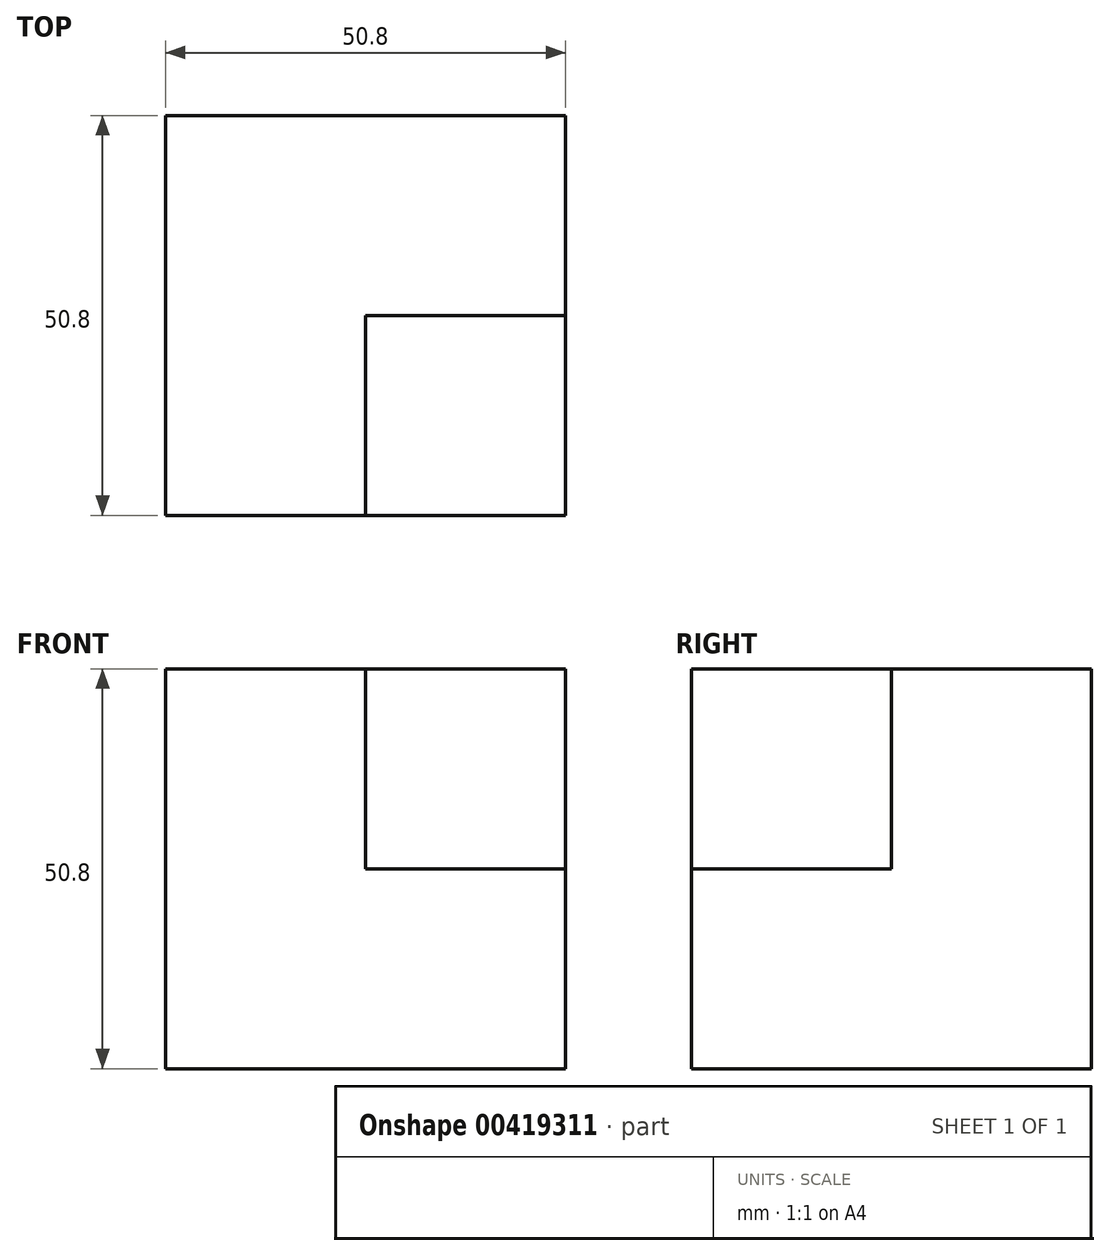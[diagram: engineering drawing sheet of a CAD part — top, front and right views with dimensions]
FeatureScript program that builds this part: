
annotation { "Feature Type Name" : "Feature", "Feature Type Description" : "" }
export const myFeature = defineFeature(function(context is Context, id is Id, definition is map)
    precondition{}
    {
        {
            var Q0;
            Q0=qCreatedBy(makeId("Front.planeOp"),FACE);
            var sketch = newSketch(context, id + "F0", { "sketchPlane" : qUnion([Q0])});
            skLineSegment(sketch, "E0.bottom", {"start": v(0, 0) * mm, "end": v(-50.8, 0) * mm});
            skLineSegment(sketch, "E0.top", {"start": v(0, 50.8) * mm, "end": v(-50.8, 50.8) * mm});
            skLineSegment(sketch, "E0.left", {"start": v(0, 0) * mm, "end": v(0, 50.8) * mm});
            skLineSegment(sketch, "E0.right", {"start": v(-50.8, 0) * mm, "end": v(-50.8, 50.8) * mm});
            skSolve(sketch);
        }
        {
            var Q0;
            Q0 = qSketchRegion(id + "F0", true);
            extrude(context, id + "F1", {"entities" : qUnion([Q0]), "depth" : 50.8 * mm});
        }
        {
            var Q0;
            Q0=makeQuery(id+"F1.opExtrude","SWEPT_FACE",FACE,{"disambiguationData":[OSD([sQuery(id+"F0.wireOp",EDGE,"E0.left")])]});
            var sketch = newSketch(context, id + "F2", { "sketchPlane" : qUnion([Q0])});
            skLineSegment(sketch, "E1", {"start": v(-25.4, 50.8) * mm, "end": v(-25.4, 25.4) * mm});
            skLineSegment(sketch, "E2", {"start": v(-25.4, 25.4) * mm, "end": v(-50.8, 25.4) * mm});
            skLineSegment(sketch, "E3", {"start": v(-50.8, 25.4) * mm, "end": v(-50.8, 50.8) * mm});
            skLineSegment(sketch, "E4", {"start": v(-50.8, 50.8) * mm, "end": v(-25.4, 50.8) * mm});
            skSolve(sketch);
        }
        {
            var Q0;
            Q0=makeQuery(id+"F2.imprint","IMPRINT",FACE,{"disambiguationData":[TD([[makeQuery(id+"F2.imprint","IMPRINT",EDGE,{"derivedFrom":sQuery(id+"F2.wireOp",EDGE,"E1")}),-1.0]])]});
            extrude(context, id + "F3", {"entities" : qUnion([Q0]), "operationType" : NewBodyOperationType.REMOVE, "oppositeDirection" : true, "depth" : 25.4 * mm});
        }
    });
